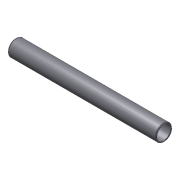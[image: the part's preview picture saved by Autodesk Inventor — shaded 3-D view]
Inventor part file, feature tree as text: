
AUTODESK INVENTOR PART (.ipt)
format: ipt  version: 2012 (Build 160160000, 160)  size: 112,128 bytes
history: native  units: in
note: dims shown in document units (in); Inventor stores cm internally (conversion verified against a paired STEP export)
features: other x42, revolve x1, sketch x1
ambient origin geometry x8: Origin, YZ Plane, XZ Plane, XY Plane, X Axis, Y Axis, Z Axis, Center Point
bodies: Solid1 (feature_tree)
feature tree (44):
  revolve  "Revolution1"  [1 undecoded]
  other  "tube_front_XY"
  other  "tube_front_YZ"
  other  "tube_front_ZX"
  other  "tube_front_X"
  other  "tube_front_Y"
  other  "tube_front_Z"
  other  "tube_front_Center"
  other  "tube_rear_XY"
  other  "tube_rear_YZ"
  other  "tube_rear_ZX"
  other  "tube_rear_X"
  other  "tube_rear_Y"
  other  "tube_rear_Z"
  other  "tube_rear_Center"
  other  "cp1_XY"
  other  "cp1_YZ"
  other  "cp1_ZX"
  other  "cp1_X"
  other  "cp1_Y"
  other  "cp1_Z"
  other  "cp1_Center"
  other  "cp2_XY"
  other  "cp2_YZ"
  other  "cp2_ZX"
  other  "cp2_X"
  other  "cp2_Y"
  other  "cp2_Z"
  other  "cp2_Center"
  other  "cp3_XY"
  other  "cp3_YZ"
  other  "cp3_ZX"
  other  "cp3_X"
  other  "cp3_Y"
  other  "cp3_Z"
  other  "cp3_Center"
  other  "cp4_XY"
  other  "cp4_YZ"
  other  "cp4_ZX"
  other  "cp4_X"
  other  "cp4_Y"
  other  "cp4_Z"
  other  "cp4_Center"
  sketch  "Sketch_1"  dims[d0=360.0deg]
note: 1 required parameter value undecoded (feature->parameter linkage not recoverable at this tier; creation-order binding heuristic only, values carry confidence <= 0.55)
